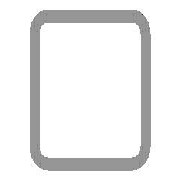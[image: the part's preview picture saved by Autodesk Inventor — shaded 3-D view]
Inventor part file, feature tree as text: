
AUTODESK INVENTOR PART (.ipt)
format: ipt  version: 2025.3 (Build 293356000, 356)  size: 134,656 bytes
history: native  units: mm (DEFAULTED — no unit token found)
features: other x4, sketch x1, plane x1
ambient origin geometry x8: Origin, YZ Plane, XZ Plane, XY Plane, X Axis, Y Axis, Z Axis, Center Point
bodies: Solid1 (feature_tree), Body (feature_tree)
feature tree (6):
  parser-record x1  (decoder bookkeeping rows leaked as tree rows — omitted from the tree; the rows remain in map.json)
  other  "Driven Length"
  other  "Start Plane"
  other  "End Plane"
  sketch  "Sketch3"  dims[d3=5400.0mm d4=0.0mm d7=6.0mm d9=80.0mm d11=80.0mm d12=3.0mm d13=-0.0mm d14=5400.0mm d15=40.0mm d16=40.0mm d17=90.0deg d18=5400.0mm]
  plane  "Work Plane3"
